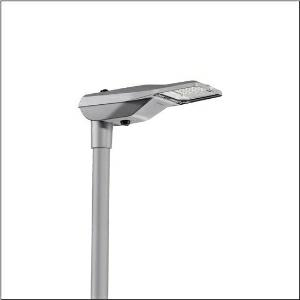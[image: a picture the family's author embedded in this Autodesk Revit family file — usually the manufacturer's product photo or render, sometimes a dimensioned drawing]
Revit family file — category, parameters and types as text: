
# Revit family: streetlight_sl_21_micro___p0_8a_5xe1u33t08db_8449
name_source: partatom
category: Lighting Fixtures
units: mm (PartAtom-declared; Revit-internal decimal feet)

## family parameters
Cut with Voids When Loaded = No
Host = Face
Light Source = No
Part Type = Normal
Room Calculation Point = No
Round Connector Dimension = Use Diameter
Shared = No

## types (1)
- --- (1 x LED, 5040 lm, 39.1 W, 3000K)
    Apparent Load = 39 VA
    CIE Flux Codes = 33 69 96 100 100
    Color Rendering = 70
    Color Temperature = 3000K
    Default Elevation = 1800 mm
    Description = Streetlight SL 21 micro, mast luminaire, primary light control with lens, of PMMA, primary optical cover: cover, of toughened safety glass, transparent, light distribution: P0.8a, light emission: direct distribution, primary light characteristic: asymmetric, installation type: post-top, side-entry, LED, High Power LED, rated luminous flux: 5.040lm, luminous efficacy: 129lm/W, light colour: 730, colour temperature: 3000K, control gear: D4i, control: pre-setting: logarithmic dimming characteristic, flexible luminous flux parameterisation, time-dependent luminous flux control, constant luminous flux control, overheat protection, mains connection: 220..240V, AC, 50/60Hz, start of lifetime: 39W, end of service life: 41W, reduction: 18W, luminaire housing, of diecast aluminium, powder-coated, SITECO metallic grey (DB 702S), corrosivity category C5 high according to DIN EN ISO 12944, multi-level sealing system, sealing non-destructively replaceable, inclination adjustable: 0°, 5°, 10°, 15°, please order mast flange separately, length: 528mm, width: 235mm, height: 110mm, mast flange for spigot size: 42mm (side-entry): 5XC10008XM4, 60/48mm (side-entry/post-top): 5XC10108XM2, 76/60mm (side-entry/post-top): 5XC10108XM1, Smart Interface below and above, protection rating (complete): IP66, insulation class (complete): insulation class II (safety insulation), certification: CE, ENEC, ENEC+, VDE, impact resistance: IK10, permissible operating ambient temperature for outdoor applications: -40..+50°C, standard-compliant lighting for roads and squares, packaging unit: 1 piece

Light Distribution: P0.8a
    Height = 110 mm
    Lamp = 1 x LED
    Lamp Light Flux = 5040 lm
    Lamp Power = 39.1 W
    Lamp count = 1
    Length = 528 mm
    Luminous efficacy = 129 lm/W
    Manufacturer = Siteco
    ModVariant = No
    Model = 5XE1U33T08DB
    Number of Poles = 1
    OnlyDefault = Yes
    Power Factor = 1
    Product Name = Streetlight SL 21 micro | P0.8a
    Product group = mast luminaire | pylon top
    ProductGroupID = 6100
    Protection Class = Protection class II
    Protection Degree = IP 66
    RLX_Detail_Level = 1
    RLX_Emergency_Light_Flux = 0 lm
    RLX_Emergency_Type = 0
    RLX_Emergency_Type_DB = No
    RlxData = <blob elided: 97945 chars, md5=7eb137cf>
    Socket = socket
    Standby Power = 0 W
    System Light Flux = 5040 lm
    System Power = 39 W
    Type Comments = factory setting: luminous flux: 100 % | dim-lin: 254 | 765 mA
    Type Image = l_1007239.jpg
    URL = http://relux.com
    VarID = @adj_080517
    Voltage = 0 V
    Weight = 0.00 kg
    Width = 235 mm

## geometry (parser evidence)
native form markers: Blend x4, Sweep x11
no freeform markers — native parametric forms only
